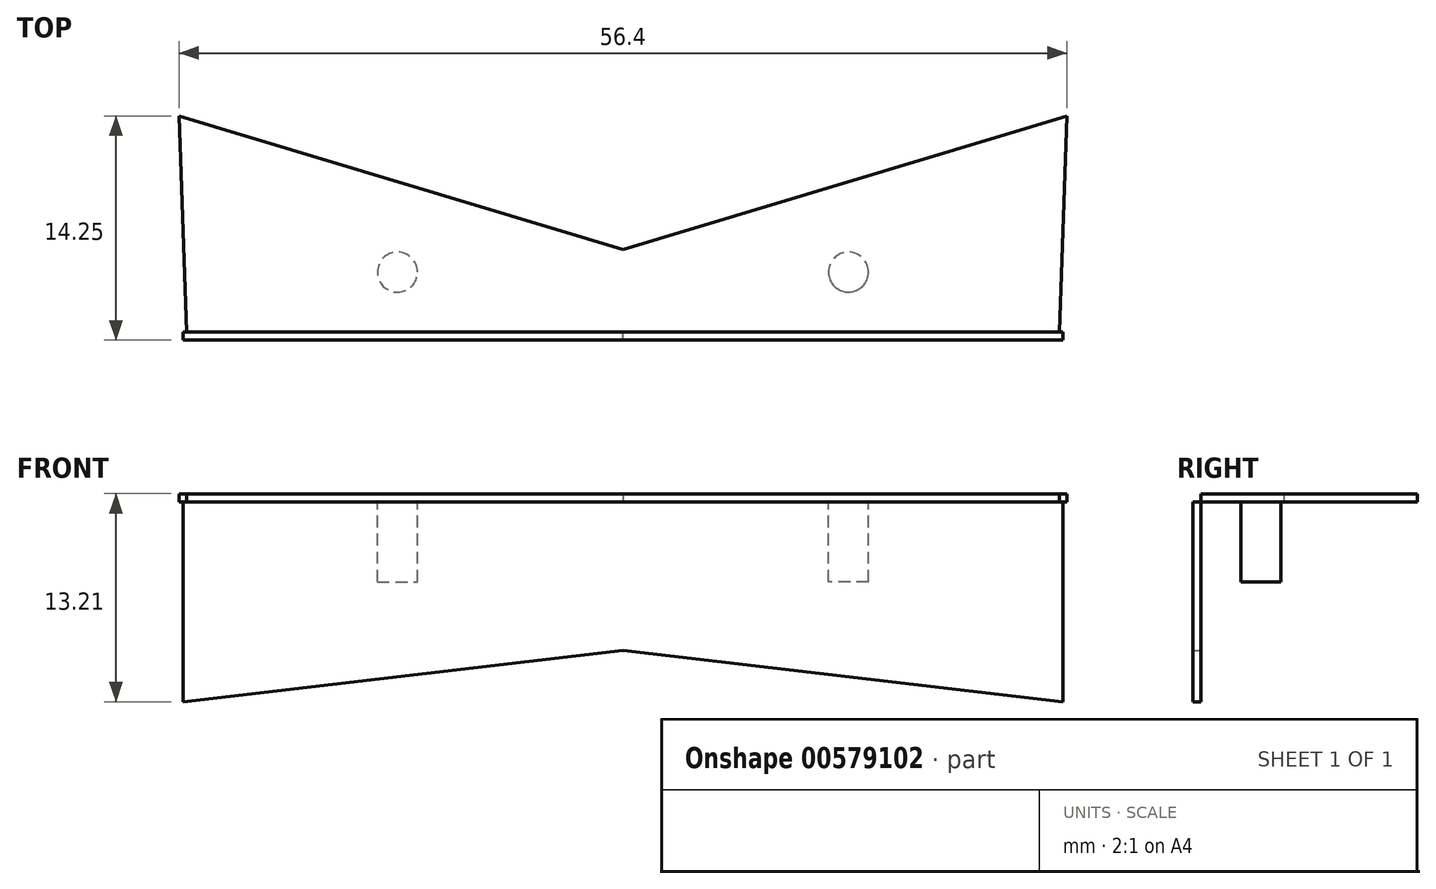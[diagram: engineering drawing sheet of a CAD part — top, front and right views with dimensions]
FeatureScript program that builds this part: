
annotation { "Feature Type Name" : "Feature", "Feature Type Description" : "" }
export const myFeature = defineFeature(function(context is Context, id is Id, definition is map)
    precondition{}
    {
        {
            var Q0;
            Q0=qCreatedBy(makeId("Front.planeOp"),FACE);
            var sketch = newSketch(context, id + "F0", { "sketchPlane" : qUnion([Q0])});
            skLineSegment(sketch, "E0", {"start": v(0, 0) * mm, "end": v(-27.94, 0) * mm});
            skLineSegment(sketch, "E1", {"start": v(-27.94, 0) * mm, "end": v(-27.94, -12.7) * mm});
            skLineSegment(sketch, "E2", {"start": v(-27.94, -12.7) * mm, "end": v(0, -9.44) * mm});
            skLineSegment(sketch, "E3", {"start": v(0, 0) * mm, "end": v(0, -9.44) * mm});
            skLineSegment(sketch, "E4.MirrorCS", {"start": v(0, 0) * mm, "end": v(27.94, 0) * mm});
            skLineSegment(sketch, "E5.MirrorCS", {"start": v(27.94, -12.7) * mm, "end": v(0, -9.44) * mm});
            skLineSegment(sketch, "E6.MirrorCS", {"start": v(27.94, 0) * mm, "end": v(27.94, -12.7) * mm});
            skSolve(sketch);
        }
        {
            var Q0;
            Q0 = qSketchRegion(id + "F0", true);
            var Q1;
            Q1=makeQuery(id+"F0.imprint","IMPRINT",FACE,{"disambiguationData":[TD([[makeQuery(id+"F0.imprint","IMPRINT",EDGE,{"derivedFrom":sQuery(id+"F0.wireOp",EDGE,"E0")}),1.0]])]});
            extrude(context, id + "F1", {"entities" : qUnion([Q0, Q1]), "depth" : 0.5 * mm, "offsetDistance" : 25.4 * mm});
        }
        {
            var Q0;
            Q0=qCreatedBy(makeId("Top.planeOp"),FACE);
            var sketch = newSketch(context, id + "F2", { "sketchPlane" : qUnion([Q0])});
            skLineSegment(sketch, "E7", {"start": v(0, 0) * mm, "end": v(0, 5.26) * mm});
            skLineSegment(sketch, "E8", {"start": v(0, 5.26) * mm, "end": v(-28.2, 13.74) * mm});
            skLineSegment(sketch, "E9", {"start": v(-28.2, 13.74) * mm, "end": v(-27.7, 0) * mm});
            skLineSegment(sketch, "E10.MirrorCS", {"start": v(0, 5.26) * mm, "end": v(28.2, 13.74) * mm});
            skLineSegment(sketch, "E11.MirrorCS", {"start": v(28.2, 13.74) * mm, "end": v(27.7, 0) * mm});
            skLineSegment(sketch, "E12", {"start": v(-27.7, 0) * mm, "end": v(0, 0) * mm});
            skLineSegment(sketch, "E13.MirrorCS", {"start": v(27.7, 0) * mm, "end": v(0, 0) * mm});
            skSolve(sketch);
        }
        {
            var Q0;
            Q0=makeQuery(id+"F2.imprint","IMPRINT",FACE,{"disambiguationData":[TD([[makeQuery(id+"F2.imprint","IMPRINT",EDGE,{"derivedFrom":sQuery(id+"F2.wireOp",EDGE,"E7")}),-1.0]])]});
            var Q1;
            Q1=makeQuery(id+"F2.imprint","IMPRINT",FACE,{"disambiguationData":[TD([[makeQuery(id+"F2.imprint","IMPRINT",EDGE,{"derivedFrom":sQuery(id+"F2.wireOp",EDGE,"E7")}),1.0]])]});
            extrude(context, id + "F3", {"entities" : qUnion([Q0, Q1]), "depth" : 0.5 * mm, "offsetDistance" : 25.4 * mm});
        }
        {
            var Q0;
            Q0=makeQuery(id+"F3.opExtrude","CAP_FACE",FACE,{"disambiguationData":[OSD([sQuery(id+"F2.wireOp",EDGE,"E8"),sQuery(id+"F2.wireOp",EDGE,"E9"),sQuery(id+"F2.wireOp",EDGE,"E10.MirrorCS"),sQuery(id+"F2.wireOp",EDGE,"E11.MirrorCS"),sQuery(id+"F2.wireOp",EDGE,"E12"),sQuery(id+"F2.wireOp",EDGE,"E13.MirrorCS")])],"isStart":true});
            var sketch = newSketch(context, id + "F4", { "sketchPlane" : qUnion([Q0])});
            skCircle(sketch, "E14", {"center": v(-14.32, -3.81) * mm, "radius": 1.27 * mm});
            skCircle(sketch, "E15.MirrorC", {"center": v(14.32, -3.81) * mm, "radius": 1.27 * mm});
            skSolve(sketch);
        }
        {
            var Q0;
            Q0 = qSketchRegion(id + "F4", true);
            extrude(context, id + "F5", {"entities" : qUnion([Q0]), "operationType" : NewBodyOperationType.ADD, "depth" : 5.08 * mm, "offsetDistance" : 25.4 * mm});
        }
    });
